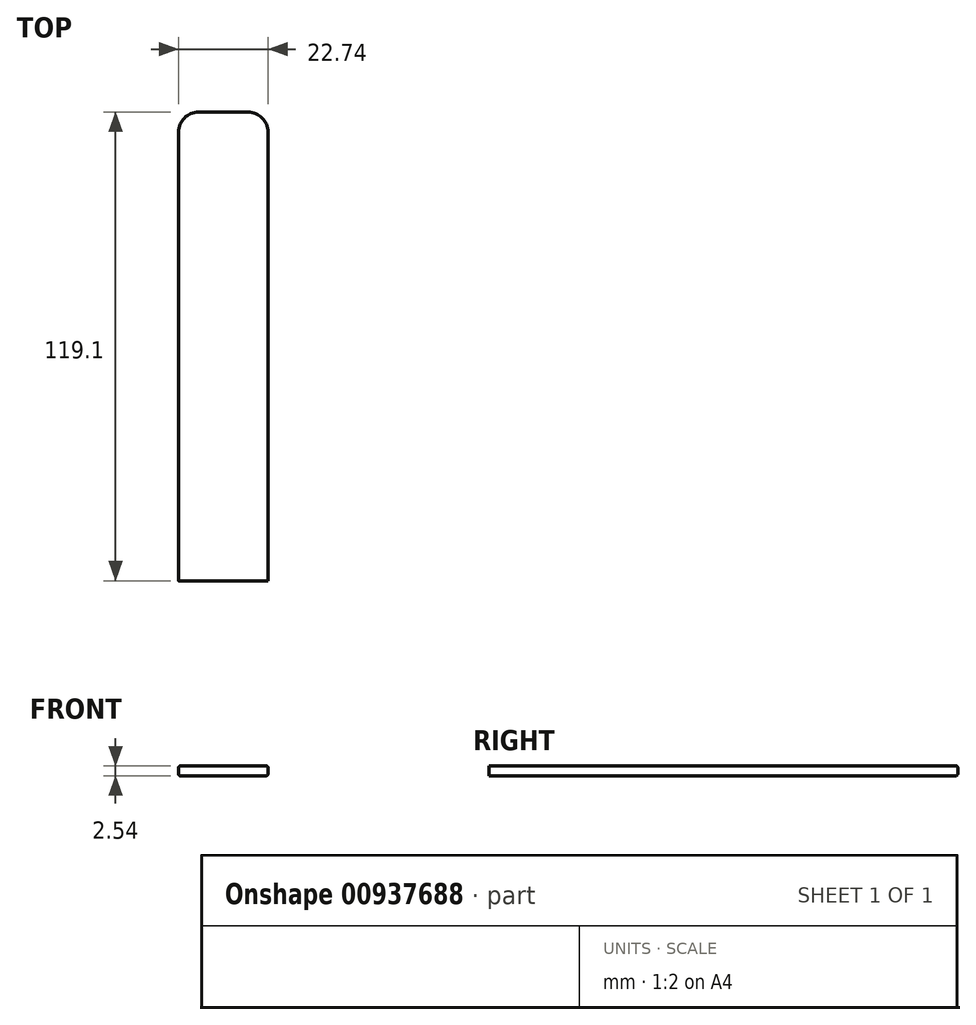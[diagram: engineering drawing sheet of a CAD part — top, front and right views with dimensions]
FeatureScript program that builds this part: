
annotation { "Feature Type Name" : "Feature", "Feature Type Description" : "" }
export const myFeature = defineFeature(function(context is Context, id is Id, definition is map)
    precondition{}
    {
        {
            var Q0;
            Q0=qCreatedBy(makeId("Top.planeOp"),FACE);
            var sketch = newSketch(context, id + "F0", { "sketchPlane" : qUnion([Q0])});
            skLineSegment(sketch, "E0.bottom", {"start": v(11.37, -59.55) * mm, "end": v(-11.37, -59.55) * mm});
            skLineSegment(sketch, "E0.top", {"start": v(11.37, 59.55) * mm, "end": v(-11.37, 59.55) * mm});
            skLineSegment(sketch, "E0.left", {"start": v(11.37, -59.55) * mm, "end": v(11.37, 59.55) * mm});
            skLineSegment(sketch, "E0.right", {"start": v(-11.37, -59.55) * mm, "end": v(-11.37, 59.55) * mm});
            skPoint(sketch, "E0.middle", {"position": v(0, 0) * mm});
            skSolve(sketch);
        }
        {
            var Q0;
            Q0=makeQuery(id+"F0.imprint","IMPRINT",FACE,{"disambiguationData":[TD([[makeQuery(id+"F0.imprint","IMPRINT",EDGE,{"derivedFrom":sQuery(id+"F0.wireOp",EDGE,"E0.bottom")}),-1.0]])]});
            extrude(context, id + "F1", {"entities" : qUnion([Q0]), "depth" : 2.54 * mm, "offsetDistance" : 25.4 * mm});
        }
        {
            var Q0;
            Q0=makeQuery(id+"F1.opExtrude","SWEPT_EDGE",EDGE,{"disambiguationData":[OSD([sQuery(id+"F0.wireOp",EDGE,"E0.top"),sQuery(id+"F0.wireOp",EDGE,"E0.left")])]});
            var Q1;
            Q1=makeQuery(id+"F1.opExtrude","SWEPT_EDGE",EDGE,{"disambiguationData":[OSD([sQuery(id+"F0.wireOp",EDGE,"E0.top"),sQuery(id+"F0.wireOp",EDGE,"E0.right")])]});
            fillet(context, id + "F2", {"entities" : qUnion([Q0, Q1]), "radius" : 5.08 * mm, "tangentPropagation" : true, "allowEdgeOverflow" : false});
        }
        {
            var Q0;
            Q0=makeQuery(id+"F1.opExtrude","CAP_EDGE",EDGE,{"disambiguationData":[OSD([sQuery(id+"F0.wireOp",EDGE,"E0.top")])],"isStart":false});
            var Q1;
            Q1=makeQuery(id+"F1.opExtrude","CAP_EDGE",EDGE,{"disambiguationData":[OSD([sQuery(id+"F0.wireOp",EDGE,"E0.top")])],"isStart":true});
            fillet(context, id + "F3", {"entities" : qUnion([Q0, Q1]), "radius" : 0.5 * mm, "tangentPropagation" : true, "allowEdgeOverflow" : false});
        }
    });
